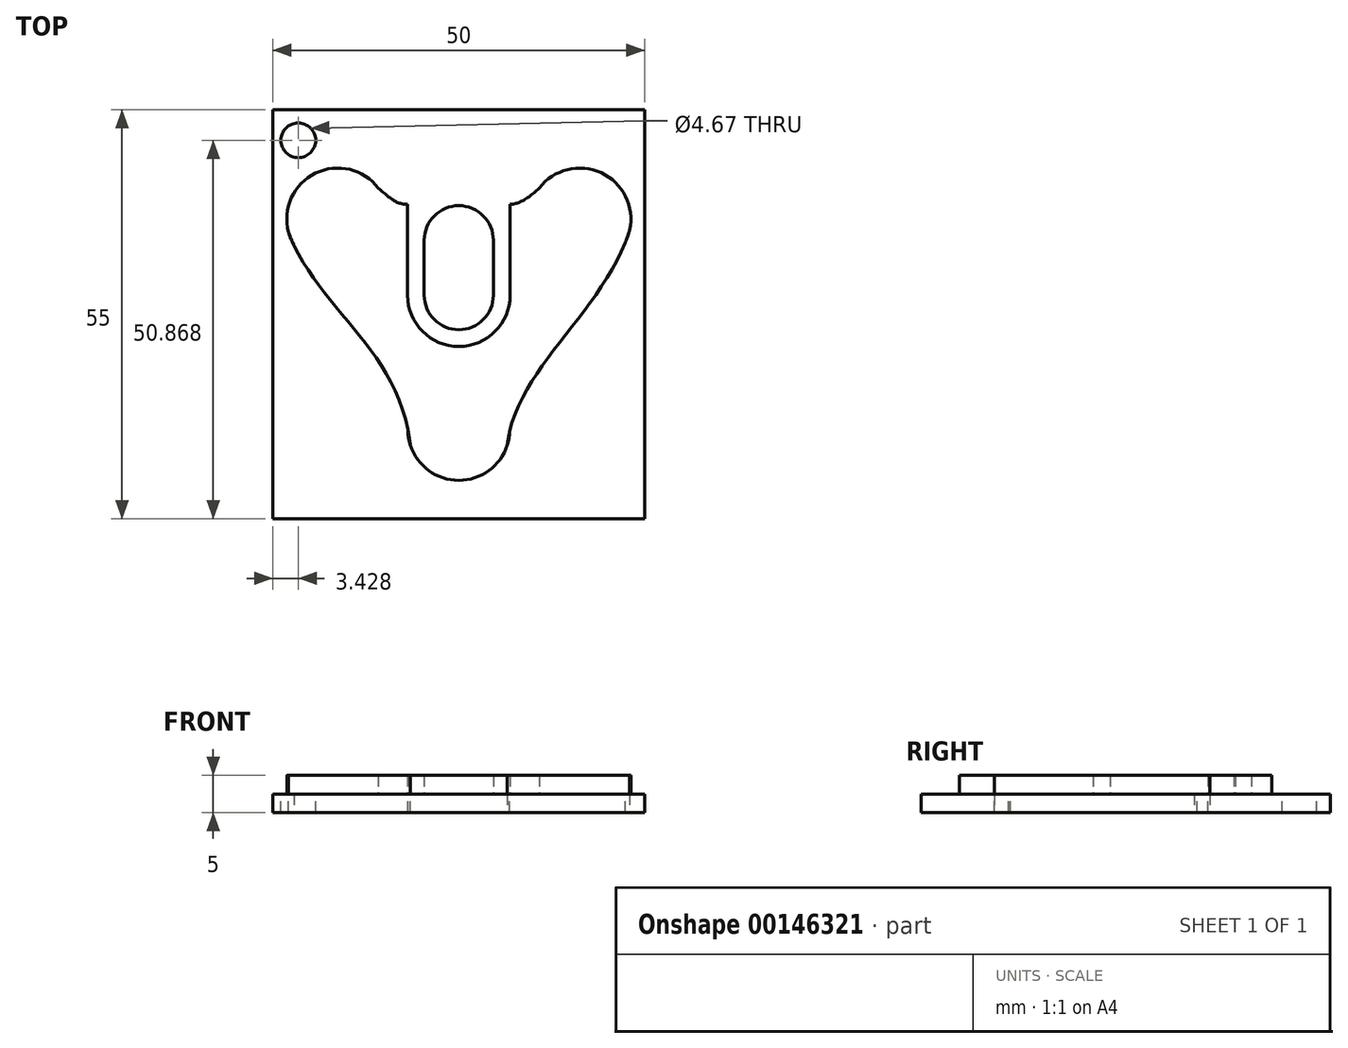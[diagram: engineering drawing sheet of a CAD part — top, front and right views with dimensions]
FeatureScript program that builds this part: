
annotation { "Feature Type Name" : "Feature", "Feature Type Description" : "" }
export const myFeature = defineFeature(function(context is Context, id is Id, definition is map)
    precondition{}
    {
        {
            var Q0;
            Q0=qCreatedBy(makeId("Top.planeOp"),FACE);
            var sketch = newSketch(context, id + "F0", { "sketchPlane" : qUnion([Q0])});
            skCircle(sketch, "E0", {"center": v(0, 22.28) * mm, "radius": 4.65 * mm});
            skCircle(sketch, "E1", {"center": v(0, 14.9) * mm, "radius": 4.65 * mm});
            skLineSegment(sketch, "E2", {"start": v(-4.65, 22.28) * mm, "end": v(-4.65, 14.9) * mm});
            skLineSegment(sketch, "E3", {"start": v(0, 17.64) * mm, "end": v(0, 10.25) * mm});
            skCircle(sketch, "E4", {"center": v(16.27, 25.13) * mm, "radius": 6.85 * mm});
            skCircle(sketch, "E5", {"center": v(-16.27, 25.13) * mm, "radius": 6.85 * mm});
            skCircle(sketch, "E6", {"center": v(0, -3.15) * mm, "radius": 6.85 * mm});
            skFitSpline(sketch, "E7", {"points": [v(-22.9, 23.38) * mm, v(-6.51, -5.27) * mm], "startDerivative": vector(11.97, -31.78) * mm, "endDerivative": vector(4.5, -39.33) * mm});
            skFitSpline(sketch, "E8", {"points": [v(22.96, 23.67) * mm, v(6.51, -5.27) * mm], "startDerivative": vector(-10.72, -33.56) * mm, "endDerivative": vector(-3.68, -31.57) * mm});
            skLineSegment(sketch, "E9", {"start": v(0, 22.28) * mm, "end": v(0, 32.32) * mm, "construction": true});
            skFitSpline(sketch, "E10", {"points": [v(-10.8, 29.27) * mm, v(-6.89, 27.1) * mm], "startDerivative": vector(4.51, -3.72) * mm, "endDerivative": vector(4.78, 0) * mm});
            skFitSpline(sketch, "E11", {"points": [v(10.8, 29.27) * mm, v(6.89, 27.1) * mm], "startDerivative": vector(-4, -3.72) * mm, "endDerivative": vector(-3.48, 0) * mm});
            skLineSegment(sketch, "E12", {"start": v(-6.89, 27.1) * mm, "end": v(-6.89, 14.9) * mm});
            skLineSegment(sketch, "E13", {"start": v(6.89, 27.1) * mm, "end": v(6.89, 14.9) * mm});
            skArc(sketch, "E14", {"start": v(-6.89, 14.9) * mm, "mid": v(0, 8) * mm, "end": v(6.89, 14.9) * mm});
            skLineSegment(sketch, "E15", {"start": v(4.65, 14.9) * mm, "end": v(4.65, 22.28) * mm});
            skLineSegment(sketch, "E16.bottom", {"start": v(-25, -15.16) * mm, "end": v(25, -15.16) * mm});
            skLineSegment(sketch, "E16.top", {"start": v(-25, 39.84) * mm, "end": v(25, 39.84) * mm});
            skLineSegment(sketch, "E16.left", {"start": v(-25, -15.16) * mm, "end": v(-25, 39.84) * mm});
            skLineSegment(sketch, "E16.right", {"start": v(25, -15.16) * mm, "end": v(25, 39.84) * mm});
            skPoint(sketch, "E16.middle", {"position": v(0, 12.34) * mm});
            skCircle(sketch, "E17", {"center": v(-21.57, 35.7) * mm, "radius": 2.34 * mm});
            skSolve(sketch);
        }
        {
            var Q0;
            Q0 = qSketchRegion(id + "F0", true);
            var Q1;
            {var subQ0=sQuery(id+"F0.wireOp",EDGE,"E7");var subQ1=sQuery(id+"F0.wireOp",EDGE,"E5");var subQ2=makeQuery(id+"F0.imprint","INTERSECT",VERTEX,{"disambiguationData":[OD(0.0)],"derivedFrom":[subQ1,subQ0]});Q1=makeQuery(id+"F0.imprint","IMPRINT",FACE,{"disambiguationData":[TD([[makeQuery(id+"F0.imprint","IMPRINT",EDGE,{"disambiguationData":[TD([[subQ2,1.0]])],"derivedFrom":subQ1}),1.0]])]});}
            var Q2;
            {var subQ5=sQuery(id+"F0.wireOp",EDGE,"E10");Q2=makeQuery(id+"F0.imprint","IMPRINT",FACE,{"disambiguationData":[TD([[makeQuery(id+"F0.imprint","IMPRINT",EDGE,{"derivedFrom":subQ5}),-1.0]])]});}
            var Q3;
            {var subQ0=sQuery(id+"F0.wireOp",EDGE,"E7");var subQ1=sQuery(id+"F0.wireOp",EDGE,"E6");var subQ2=makeQuery(id+"F0.imprint","INTERSECT",VERTEX,{"disambiguationData":[OD(0.0)],"derivedFrom":[subQ1,subQ0]});Q3=makeQuery(id+"F0.imprint","IMPRINT",FACE,{"disambiguationData":[TD([[makeQuery(id+"F0.imprint","IMPRINT",EDGE,{"disambiguationData":[TD([[subQ2,-1.0]])],"derivedFrom":subQ1}),1.0]])]});}
            var Q4;
            {var subQ0=sQuery(id+"F0.wireOp",EDGE,"E0");var subQ1=makeQuery(id+"F0.imprint","INTERSECT",VERTEX,{"derivedFrom":[subQ0,sQuery(id+"F0.wireOp",EDGE,"E2")]});Q4=makeQuery(id+"F0.imprint","IMPRINT",FACE,{"disambiguationData":[TD([[makeQuery(id+"F0.imprint","IMPRINT",EDGE,{"disambiguationData":[TD([[subQ1,1.0]])],"derivedFrom":subQ0}),1.0]])]});}
            var Q5;
            {var subQ0=sQuery(id+"F0.wireOp",EDGE,"E3");Q5=makeQuery(id+"F0.imprint","IMPRINT",FACE,{"disambiguationData":[TD([[makeQuery(id+"F0.imprint","IMPRINT",EDGE,{"derivedFrom":subQ0}),-1.0]])]});}
            var Q6;
            {var subQ0=sQuery(id+"F0.wireOp",EDGE,"E2");Q6=makeQuery(id+"F0.imprint","IMPRINT",FACE,{"disambiguationData":[TD([[makeQuery(id+"F0.imprint","IMPRINT",EDGE,{"derivedFrom":subQ0}),1.0]])]});}
            var Q7;
            {var subQ0=sQuery(id+"F0.wireOp",EDGE,"E0");var subQ1=makeQuery(id+"F0.imprint","INTERSECT",VERTEX,{"derivedFrom":[subQ0,sQuery(id+"F0.wireOp",EDGE,"E3")]});Q7=makeQuery(id+"F0.imprint","IMPRINT",FACE,{"disambiguationData":[TD([[makeQuery(id+"F0.imprint","IMPRINT",EDGE,{"disambiguationData":[TD([[subQ1,1.0]])],"derivedFrom":subQ0}),1.0]])]});}
            var Q8;
            {var subQ0=sQuery(id+"F0.wireOp",EDGE,"E3");Q8=makeQuery(id+"F0.imprint","IMPRINT",FACE,{"disambiguationData":[TD([[makeQuery(id+"F0.imprint","IMPRINT",EDGE,{"derivedFrom":subQ0}),1.0]])]});}
            var Q9;
            {var subQ0=sQuery(id+"F0.wireOp",EDGE,"E4");var subQ1=makeQuery(id+"F0.imprint","INTERSECT",VERTEX,{"derivedFrom":[subQ0,sQuery(id+"F0.wireOp",EDGE,"E11")]});Q9=makeQuery(id+"F0.imprint","IMPRINT",FACE,{"disambiguationData":[TD([[makeQuery(id+"F0.imprint","IMPRINT",EDGE,{"disambiguationData":[TD([[subQ1,-1.0]])],"derivedFrom":subQ0}),1.0]])]});}
            var Q10;
            {var subQ0=sQuery(id+"F0.wireOp",EDGE,"E15");Q10=makeQuery(id+"F0.imprint","IMPRINT",FACE,{"disambiguationData":[TD([[makeQuery(id+"F0.imprint","IMPRINT",EDGE,{"derivedFrom":subQ0}),1.0]])]});}
            extrude(context, id + "F1", {"entities" : qUnion([Q0, Q1, Q2, Q3, Q4, Q5, Q6, Q7, Q8, Q9, Q10]), "oppositeDirection" : true, "depth" : 2.5 * mm});
        }
        {
            var Q0;
            {var subQ0=sQuery(id+"F0.wireOp",EDGE,"E7");var subQ1=sQuery(id+"F0.wireOp",EDGE,"E5");var subQ2=makeQuery(id+"F0.imprint","INTERSECT",VERTEX,{"disambiguationData":[OD(0.0)],"derivedFrom":[subQ1,subQ0]});Q0=makeQuery(id+"F0.imprint","IMPRINT",FACE,{"disambiguationData":[TD([[makeQuery(id+"F0.imprint","IMPRINT",EDGE,{"disambiguationData":[TD([[subQ2,1.0]])],"derivedFrom":subQ1}),1.0]])]});}
            var Q1;
            {var subQ5=sQuery(id+"F0.wireOp",EDGE,"E10");Q1=makeQuery(id+"F0.imprint","IMPRINT",FACE,{"disambiguationData":[TD([[makeQuery(id+"F0.imprint","IMPRINT",EDGE,{"derivedFrom":subQ5}),-1.0]])]});}
            var Q2;
            {var subQ0=sQuery(id+"F0.wireOp",EDGE,"E7");var subQ1=sQuery(id+"F0.wireOp",EDGE,"E6");var subQ2=makeQuery(id+"F0.imprint","INTERSECT",VERTEX,{"disambiguationData":[OD(0.0)],"derivedFrom":[subQ1,subQ0]});Q2=makeQuery(id+"F0.imprint","IMPRINT",FACE,{"disambiguationData":[TD([[makeQuery(id+"F0.imprint","IMPRINT",EDGE,{"disambiguationData":[TD([[subQ2,-1.0]])],"derivedFrom":subQ1}),1.0]])]});}
            var Q3;
            {var subQ0=sQuery(id+"F0.wireOp",EDGE,"E4");var subQ1=makeQuery(id+"F0.imprint","INTERSECT",VERTEX,{"derivedFrom":[subQ0,sQuery(id+"F0.wireOp",EDGE,"E11")]});Q3=makeQuery(id+"F0.imprint","IMPRINT",FACE,{"disambiguationData":[TD([[makeQuery(id+"F0.imprint","IMPRINT",EDGE,{"disambiguationData":[TD([[subQ1,-1.0]])],"derivedFrom":subQ0}),1.0]])]});}
            var Q4;
            {var subQ0=sQuery(id+"F0.wireOp",EDGE,"E0");var subQ1=makeQuery(id+"F0.imprint","INTERSECT",VERTEX,{"derivedFrom":[subQ0,sQuery(id+"F0.wireOp",EDGE,"E2")]});Q4=makeQuery(id+"F0.imprint","IMPRINT",FACE,{"disambiguationData":[TD([[makeQuery(id+"F0.imprint","IMPRINT",EDGE,{"disambiguationData":[TD([[subQ1,1.0]])],"derivedFrom":subQ0}),1.0]])]});}
            var Q5;
            {var subQ0=sQuery(id+"F0.wireOp",EDGE,"E3");Q5=makeQuery(id+"F0.imprint","IMPRINT",FACE,{"disambiguationData":[TD([[makeQuery(id+"F0.imprint","IMPRINT",EDGE,{"derivedFrom":subQ0}),-1.0]])]});}
            var Q6;
            {var subQ0=sQuery(id+"F0.wireOp",EDGE,"E3");Q6=makeQuery(id+"F0.imprint","IMPRINT",FACE,{"disambiguationData":[TD([[makeQuery(id+"F0.imprint","IMPRINT",EDGE,{"derivedFrom":subQ0}),1.0]])]});}
            var Q7;
            {var subQ0=sQuery(id+"F0.wireOp",EDGE,"E2");Q7=makeQuery(id+"F0.imprint","IMPRINT",FACE,{"disambiguationData":[TD([[makeQuery(id+"F0.imprint","IMPRINT",EDGE,{"derivedFrom":subQ0}),1.0]])]});}
            var Q8;
            {var subQ0=sQuery(id+"F0.wireOp",EDGE,"E15");Q8=makeQuery(id+"F0.imprint","IMPRINT",FACE,{"disambiguationData":[TD([[makeQuery(id+"F0.imprint","IMPRINT",EDGE,{"derivedFrom":subQ0}),1.0]])]});}
            var Q9;
            {var subQ0=sQuery(id+"F0.wireOp",EDGE,"E0");var subQ1=makeQuery(id+"F0.imprint","INTERSECT",VERTEX,{"derivedFrom":[subQ0,sQuery(id+"F0.wireOp",EDGE,"E3")]});Q9=makeQuery(id+"F0.imprint","IMPRINT",FACE,{"disambiguationData":[TD([[makeQuery(id+"F0.imprint","IMPRINT",EDGE,{"disambiguationData":[TD([[subQ1,1.0]])],"derivedFrom":subQ0}),1.0]])]});}
            extrude(context, id + "F2", {"entities" : qUnion([Q0, Q1, Q2, Q3, Q4, Q5, Q6, Q7, Q8, Q9]), "operationType" : NewBodyOperationType.ADD, "depth" : 2.5 * mm});
        }
    });
